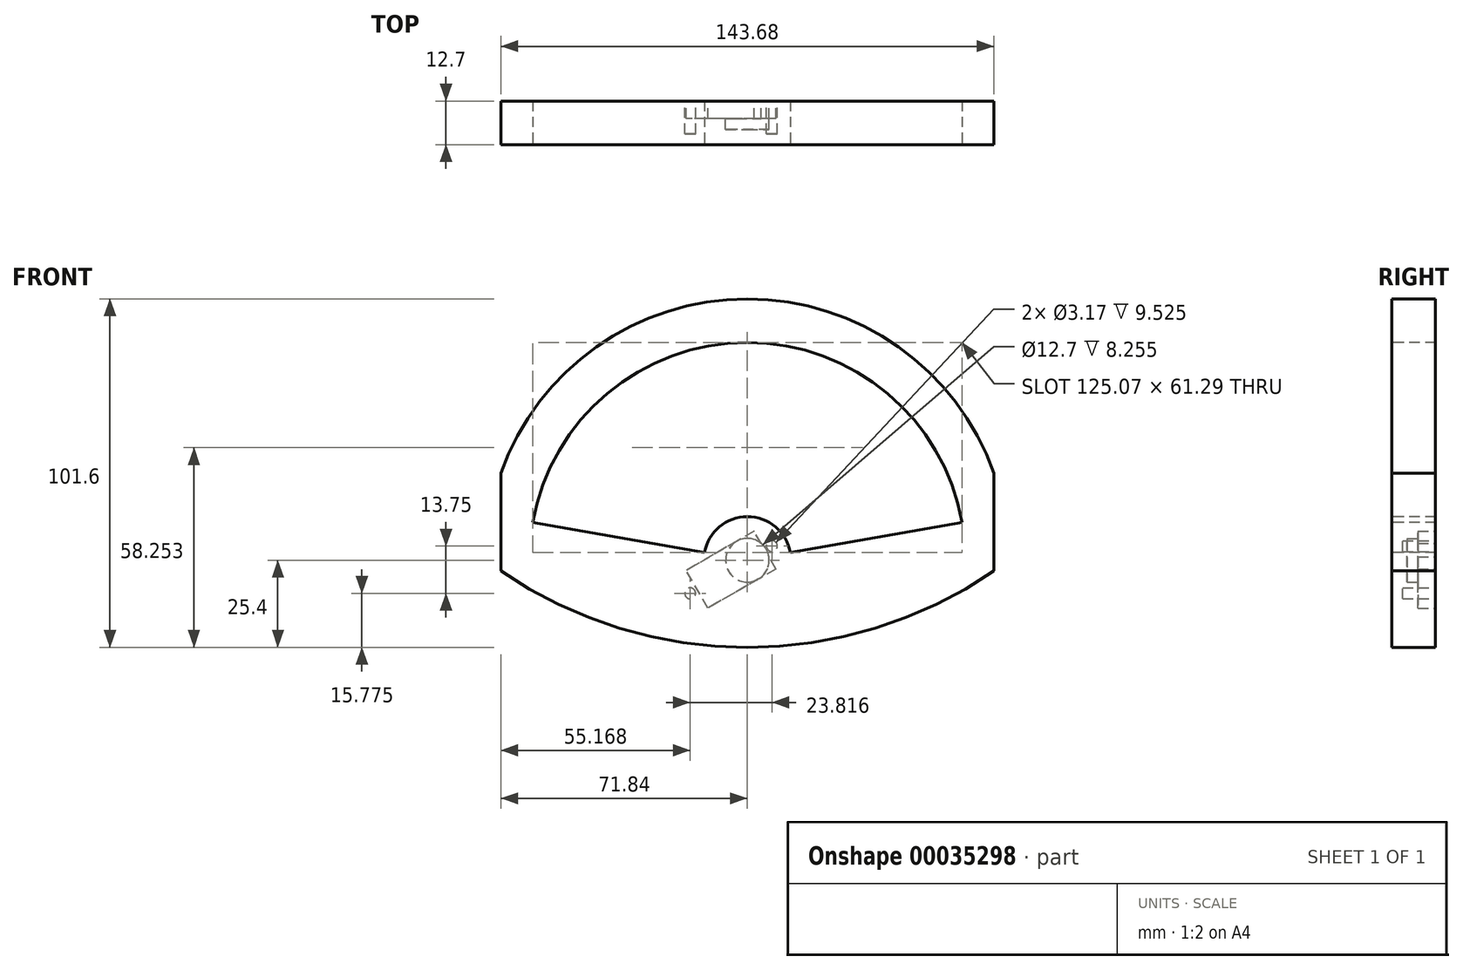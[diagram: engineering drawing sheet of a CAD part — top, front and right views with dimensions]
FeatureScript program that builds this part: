
annotation { "Feature Type Name" : "Feature", "Feature Type Description" : "" }
export const myFeature = defineFeature(function(context is Context, id is Id, definition is map)
    precondition{}
    {
        {
            var Q0;
            Q0=qCreatedBy(makeId("Front.planeOp"),FACE);
            var sketch = newSketch(context, id + "F0", { "sketchPlane" : qUnion([Q0])});
            skArc(sketch, "E0", {"start": v(0, 50.8) * mm, "mid": v(-44, 36.82) * mm, "end": v(-71.84, 0) * mm});
            skLineSegment(sketch, "E1", {"start": v(-71.84, 0) * mm, "end": v(-71.84, -28.53) * mm});
            skArc(sketch, "E2.MirrorCS", {"start": v(0, 50.8) * mm, "mid": v(44, 36.82) * mm, "end": v(71.84, 0) * mm});
            skLineSegment(sketch, "E3.MirrorCS", {"start": v(71.84, 0) * mm, "end": v(71.84, -28.53) * mm});
            skArc(sketch, "E4", {"start": v(-71.84, -28.53) * mm, "mid": v(-37.6, -45.1) * mm, "end": v(0, -50.8) * mm});
            skArc(sketch, "E5.MirrorCS", {"start": v(71.84, -28.53) * mm, "mid": v(37.6, -45.1) * mm, "end": v(0, -50.8) * mm});
            skSolve(sketch);
        }
        {
            var Q0;
            Q0=qCreatedBy(makeId("Front.planeOp"),FACE);
            var sketch = newSketch(context, id + "F1", { "sketchPlane" : qUnion([Q0])});
            skArc(sketch, "E6.1", {"start": v(0, 38.1) * mm, "mid": v(-40.82, 23.24) * mm, "end": v(-62.54, -14.37) * mm});
            skArc(sketch, "E7", {"start": v(12.5, -23.2) * mm, "mid": v(0, -12.7) * mm, "end": v(-12.5, -23.2) * mm});
            skArc(sketch, "E8.MirrorCS", {"start": v(0, 38.1) * mm, "mid": v(40.82, 23.24) * mm, "end": v(62.54, -14.37) * mm});
            skLineSegment(sketch, "E9", {"start": v(-62.54, -14.37) * mm, "end": v(-12.5, -23.2) * mm});
            skLineSegment(sketch, "E10.MirrorCS", {"start": v(62.54, -14.37) * mm, "end": v(12.5, -23.2) * mm});
            skSolve(sketch);
        }
        {
            var Q0;
            Q0=qCreatedBy(makeId("Front.planeOp"),FACE);
            var sketch = newSketch(context, id + "F2", { "sketchPlane" : qUnion([Q0])});
            skCircle(sketch, "E11", {"center": v(0, -25.4) * mm, "radius": 6.35 * mm});
            skSolve(sketch);
        }
        {
            var Q0;
            Q0=qCreatedBy(makeId("Front.planeOp"),FACE);
            var sketch = newSketch(context, id + "F3", { "sketchPlane" : qUnion([Q0])});
            skCircle(sketch, "E12", {"center": v(7.14, -21.28) * mm, "radius": 1.59 * mm});
            skCircle(sketch, "E13", {"center": v(-16.67, -35.03) * mm, "radius": 1.59 * mm});
            skLineSegment(sketch, "E14", {"start": v(7.14, -21.28) * mm, "end": v(-16.67, -35.03) * mm, "construction": true});
            skSolve(sketch);
        }
        {
            var Q0;
            Q0=qSketchRegion(id+"F0",true);
            extrude(context, id + "F4", {"entities" : qUnion([Q0]), "depth" : 12.7 * mm});
        }
        {
            var Q0;
            Q0=qSketchRegion(id+"F1",true);
            extrude(context, id + "F5", {"entities" : qUnion([Q0]), "operationType" : NewBodyOperationType.REMOVE, "endBound" : BoundingType.SYMMETRIC, "oppositeDirection" : true, "depth" : 25.4 * mm});
        }
        {
            var Q0;
            Q0=qSketchRegion(id+"F2",true);
            extrude(context, id + "F6", {"entities" : qUnion([Q0]), "operationType" : NewBodyOperationType.REMOVE, "depth" : 8.25 * mm});
        }
        {
            var Q0;
            Q0=qSketchRegion(id+"F3",true);
            extrude(context, id + "F7", {"entities" : qUnion([Q0]), "operationType" : NewBodyOperationType.REMOVE, "depth" : 9.52 * mm});
        }
        {
            var Q0;
            Q0=makeQuery(id+"F4.opExtrude","CAP_FACE",FACE,{"disambiguationData":[OSD([sQuery(id+"F0.wireOp",EDGE,"E0"),sQuery(id+"F0.wireOp",EDGE,"E1"),sQuery(id+"F0.wireOp",EDGE,"E2.MirrorCS"),sQuery(id+"F0.wireOp",EDGE,"E3.MirrorCS"),sQuery(id+"F0.wireOp",EDGE,"E4"),sQuery(id+"F0.wireOp",EDGE,"E5.MirrorCS")])],"isStart":true});
            var sketch = newSketch(context, id + "F8", { "sketchPlane" : qUnion([Q0])});
            skLineSegment(sketch, "E15.bottom", {"start": v(-8.31, -27.93) * mm, "end": v(11.49, -39.36) * mm});
            skLineSegment(sketch, "E15.top", {"start": v(-1.96, -16.94) * mm, "end": v(17.84, -28.37) * mm});
            skLineSegment(sketch, "E15.left", {"start": v(-8.31, -27.93) * mm, "end": v(-1.96, -16.94) * mm});
            skLineSegment(sketch, "E15.right", {"start": v(11.49, -39.36) * mm, "end": v(17.84, -28.37) * mm});
            skLineSegment(sketch, "E16", {"start": v(-7.14, -21.28) * mm, "end": v(16.67, -35.03) * mm, "construction": true});
            skLineSegment(sketch, "E17", {"start": v(7.94, -22.65) * mm, "end": v(1.59, -33.65) * mm, "construction": true});
            skPoint(sketch, "E18", {"position": v(4.76, -28.15) * mm});
            skSolve(sketch);
        }
        {
            var Q0;
            Q0=qSketchRegion(id+"F8",true);
            extrude(context, id + "F9", {"entities" : qUnion([Q0]), "operationType" : NewBodyOperationType.REMOVE, "oppositeDirection" : true, "depth" : 5.08 * mm});
        }
    });
